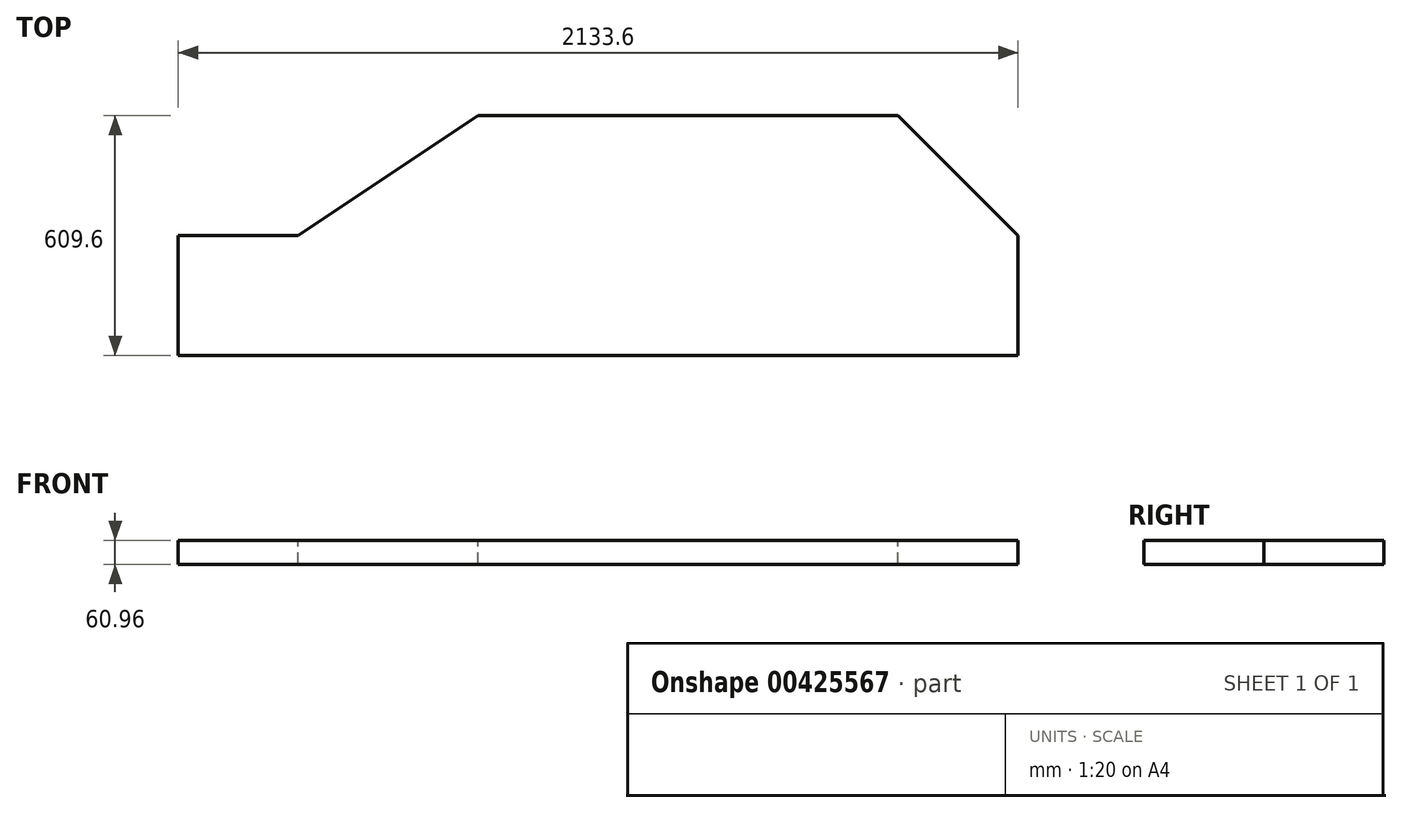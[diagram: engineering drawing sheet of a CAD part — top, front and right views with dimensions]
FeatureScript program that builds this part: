
annotation { "Feature Type Name" : "Feature", "Feature Type Description" : "" }
export const myFeature = defineFeature(function(context is Context, id is Id, definition is map)
    precondition{}
    {
        {
            var Q0;
            Q0=qCreatedBy(makeId("Top.planeOp"),FACE);
            var sketch = newSketch(context, id + "F0", { "sketchPlane" : qUnion([Q0])});
            skLineSegment(sketch, "E0.bottom", {"start": v(762, 304.8) * mm, "end": v(-304.8, 304.8) * mm});
            skLineSegment(sketch, "E0.top", {"start": v(1066.8, -304.8) * mm, "end": v(-1066.8, -304.8) * mm});
            skLineSegment(sketch, "E0.left", {"start": v(1066.8, 0) * mm, "end": v(1066.8, -304.8) * mm});
            skLineSegment(sketch, "E0.right", {"start": v(-1066.8, 0) * mm, "end": v(-1066.8, -304.8) * mm});
            skPoint(sketch, "E0.middle", {"position": v(0, 0) * mm});
            skLineSegment(sketch, "E1", {"start": v(-1066.8, -304.8) * mm, "end": v(-1066.8, 0) * mm});
            skLineSegment(sketch, "E2", {"start": v(-1066.8, 0) * mm, "end": v(-762, 0) * mm});
            skLineSegment(sketch, "E3", {"start": v(-762, 0) * mm, "end": v(-304.8, 304.8) * mm});
            skLineSegment(sketch, "E4", {"start": v(-304.8, 304.8) * mm, "end": v(762, 304.8) * mm});
            skLineSegment(sketch, "E5", {"start": v(762, 304.8) * mm, "end": v(1066.8, 0) * mm});
            skPoint(sketch, "E6.orphan", {"position": v(-1066.8, 304.8) * mm});
            skPoint(sketch, "E7.orphan", {"position": v(1066.8, 304.8) * mm});
            skSolve(sketch);
        }
        {
            var Q0;
            Q0 = qSketchRegion(id + "F0", true);
            extrude(context, id + "F1", {"entities" : qUnion([Q0]), "oppositeDirection" : true, "depth" : 60.96 * mm});
        }
    });
